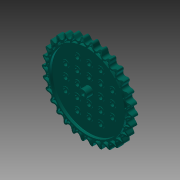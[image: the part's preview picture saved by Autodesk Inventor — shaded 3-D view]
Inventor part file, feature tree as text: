
AUTODESK INVENTOR PART (.ipt)
format: ipt  version: 2013 (Build 170138000, 138)  size: 2,566,144 bytes
history: native  units: in
note: dims shown in document units (in); Inventor stores cm internally (conversion verified against a paired STEP export)
features: sketch x8, extrude x7, fillet x2, plane x1, revolve x1, hole x1, pattern_circular x1, mirror x1, other x1
ambient origin geometry x8: Origin, YZ Plane, XZ Plane, XY Plane, X Axis, Y Axis, Z Axis, Center Point
bodies: Solid1 (feature_tree)
feature tree (23):
  sketch  "Sketch1"  dims[d0=0.3in d1=0.0in d2=3.169in]
  extrude  "Extrusion1"  Depth=3.169in
  extrude  "Extrusion2"  Depth=0.354in
  extrude  "Extrusion3"  Depth=0.029in
  plane  "Work Plane1"
  revolve  "Revolution1"  Angle=90.0deg
  extrude  "Extrusion4"  Depth=0.012in
  fillet  "Fillet1"  Radius=0.012in
  fillet  "Fillet2"  Radius=0.315in
  hole  "Hole1"  [1 undecoded]
  extrude  "Extrusion5"  Depth=0.227in TaperAngle=0.0deg
  pattern_circular  "Circular Pattern1"  [2 undecoded]
  mirror  "Mirror1"
  extrude  "Extrusion6"  TaperAngle=0.0deg  [1 undecoded]
  sketch  "Sketch2"  dims[d3=0.111in d4=0.0in d5=0.354in]
  sketch  "Sketch3"  dims[d6=0.273in d7=0.0in d8=0.029in]
  sketch  "Sketch4"  dims[d9=0.165in d10=90.0deg]
  sketch  "Sketch5"  dims[d11=0.111in d12=0.0in d13=0.012in d14=0.012in]
  sketch  "Sketch6"  dims[d15=0.175in d16=0.75in d17=0.375in d18=0.25in d19=0.5635in d20=1.0in d21=0.8108in d22=0.315in]
  sketch  "Sketch7"  dims[d23=0.023in d24=0.0in d25=11.811in d26=360.0deg]
  sketch  "Sketch8"  dims[d28=0.023in d29=0.0in d30=0.227in d31=0.0in d32=0.0in d33=0.0in]
  other  "Srf1"
  extrude  "ExtrusionSrf1"  [1 undecoded]
note: 5 required parameter values undecoded (feature->parameter linkage not recoverable at this tier; creation-order binding heuristic only, values carry confidence <= 0.55)
